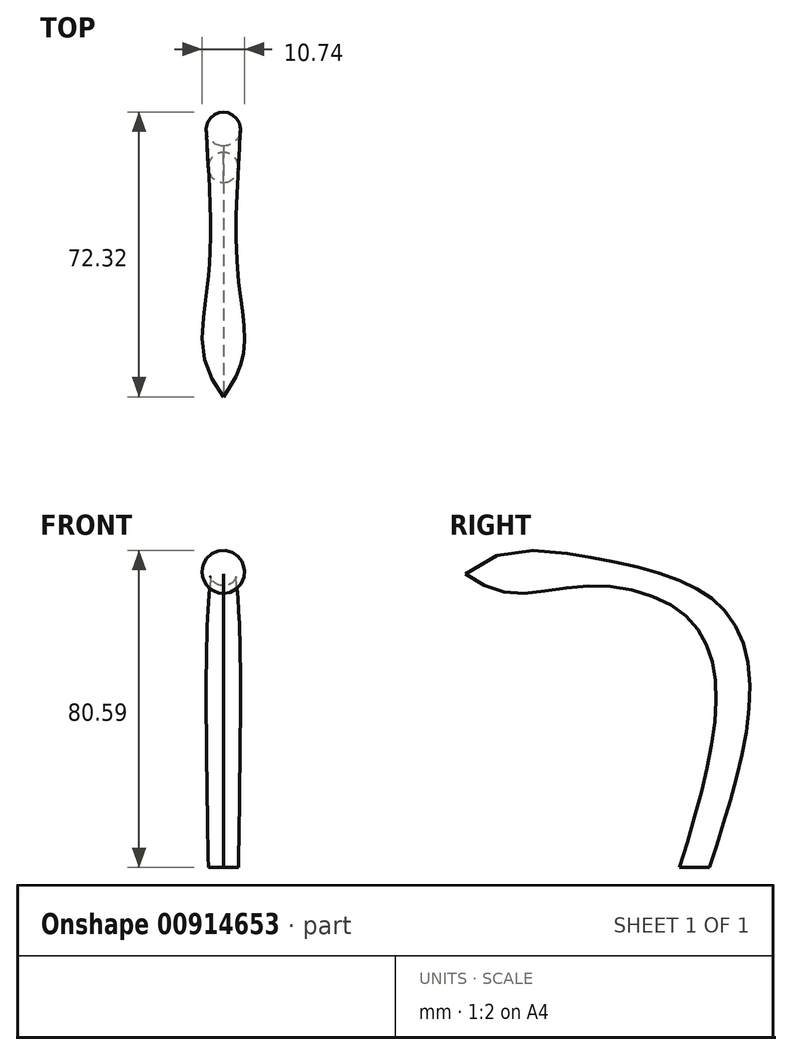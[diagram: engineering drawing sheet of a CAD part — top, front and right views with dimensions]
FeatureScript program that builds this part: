
annotation { "Feature Type Name" : "Feature", "Feature Type Description" : "" }
export const myFeature = defineFeature(function(context is Context, id is Id, definition is map)
    precondition{}
    {
        {
            var Q0;
            Q0=qCreatedBy(makeId("Top.planeOp"),FACE);
            var sketch = newSketch(context, id + "F0", { "sketchPlane" : qUnion([Q0])});
            skCircle(sketch, "E0", {"center": v(0, 0) * mm, "radius": 3.81 * mm});
            skSolve(sketch);
        }
        {
            var Q0;
            Q0=qCreatedBy(makeId("Right.planeOp"),FACE);
            var sketch = newSketch(context, id + "F1", { "sketchPlane" : qUnion([Q0])});
            skFitSpline(sketch, "E1", {"points": [v(0, 0) * mm, v(0, 66.6) * mm, v(-51.9, 74.72) * mm], "startDerivative": vector(29.22, 154.47) * mm, "endDerivative": vector(-136.3, -8.24) * mm});
            skFitSpline(sketch, "E2", {"points": [v(-51.9, 74.72) * mm, v(-57.65, 74.72) * mm], "startDerivative": vector(-5.75, 0) * mm, "endDerivative": vector(-5.75, 0) * mm});
            skPoint(sketch, "E3", {"position": v(-28.35, 75.54) * mm});
            skSolve(sketch);
        }
        {
            var Q0;
            Q0=sQuery(id+"F1.wireOp",VERTEX,"E1.1.internal");
            var Q1;
            Q1=sQuery(id+"F1.wireOp",EDGE,"E1");
            var Q2;
            Q2 = qBodyType(qCreatedBy(id + "F3" ,EDGE), BodyType.WIRE);
            cPlane(context, id + "F2", {"entities" : qUnion([Q0, Q1, Q2]), "cplaneType" : CPlaneType.CURVE_POINT, "offset" : 25.4 * mm, "width" : 152.4 * mm, "height" : 152.4 * mm});
        }
        {
            var Q0;
            Q0=qCreatedBy(id+"F2.planeOp",FACE);
            var sketch = newSketch(context, id + "F3", { "sketchPlane" : qUnion([Q0])});
            skCircle(sketch, "E4", {"center": v(0, 43.56) * mm, "radius": 3.81 * mm});
            skSolve(sketch);
        }
        {
            var Q0;
            Q0=sQuery(id+"F1.wireOp",VERTEX,"E1.end");
            var Q1;
            Q1=sQuery(id+"F1.wireOp",EDGE,"E1");
            cPlane(context, id + "F4", {"entities" : qUnion([Q0, Q1]), "cplaneType" : CPlaneType.CURVE_POINT, "offset" : 25.4 * mm, "width" : 152.4 * mm, "height" : 152.4 * mm});
        }
        {
            var Q0;
            Q0=qCreatedBy(id+"F4.planeOp",FACE);
            var sketch = newSketch(context, id + "F5", { "sketchPlane" : qUnion([Q0])});
            skCircle(sketch, "E5", {"center": v(0, 77.64) * mm, "radius": 3.81 * mm});
            skSolve(sketch);
        }
        {
            var Q0;
            Q0=qCreatedBy(id+"F4.planeOp",FACE);
            cPlane(context, id + "F6", {"entities" : qUnion([Q0]), "cplaneType" : CPlaneType.OFFSET, "offset" : 6.35 * mm, "width" : 152.4 * mm, "height" : 152.4 * mm});
        }
        {
            var Q0;
            Q0=qCreatedBy(id+"F6.planeOp",FACE);
            var sketch = newSketch(context, id + "F7", { "sketchPlane" : qUnion([Q0])});
            skCircle(sketch, "E6", {"center": v(0, 78) * mm, "radius": 1.27 * mm});
            skSolve(sketch);
        }
        {
            var Q0;
            Q0=sQuery(id+"F1.wireOp",VERTEX,"E3");
            var Q1;
            Q1=sQuery(id+"F1.wireOp",EDGE,"E1");
            cPlane(context, id + "F8", {"entities" : qUnion([Q0, Q1]), "cplaneType" : CPlaneType.CURVE_POINT, "offset" : 25.4 * mm, "width" : 152.4 * mm, "height" : 152.4 * mm});
        }
        {
            var Q0;
            Q0=qCreatedBy(id+"F8.planeOp",FACE);
            var sketch = newSketch(context, id + "F9", { "sketchPlane" : qUnion([Q0])});
            skCircle(sketch, "E7", {"center": v(0, 74.69) * mm, "radius": 3.81 * mm});
            skSolve(sketch);
        }
        {
            var Q0;
            Q0=makeQuery(id+"F0.imprint","IMPRINT",FACE,{"disambiguationData":[TD([[makeQuery(id+"F0.imprint","IMPRINT",EDGE,{"derivedFrom":sQuery(id+"F0.wireOp",EDGE,"E0")}),1.0]])]});
            var Q1;
            Q1=makeQuery(id+"F3.imprint","IMPRINT",FACE,{"disambiguationData":[TD([[makeQuery(id+"F3.imprint","IMPRINT",EDGE,{"derivedFrom":sQuery(id+"F3.wireOp",EDGE,"E4")}),1.0]])]});
            var Q2;
            Q2=makeQuery(id+"F9.imprint","IMPRINT",FACE,{"disambiguationData":[TD([[makeQuery(id+"F9.imprint","IMPRINT",EDGE,{"derivedFrom":sQuery(id+"F9.wireOp",EDGE,"E7")}),1.0]])]});
            var Q3;
            Q3=makeQuery(id+"F5.imprint","IMPRINT",FACE,{"disambiguationData":[TD([[makeQuery(id+"F5.imprint","IMPRINT",EDGE,{"derivedFrom":sQuery(id+"F5.wireOp",EDGE,"E5")}),1.0]])]});
            var Q4;
            Q4=sQuery(id+"F7.wireOp",VERTEX,"E6.center");
            loft(context, id + "F10", {"sheetProfilesArray" : [{ "sheetProfileEntities" : qUnion([Q0]) }, { "sheetProfileEntities" : qUnion([Q1]) }, { "sheetProfileEntities" : qUnion([Q2]) }, { "sheetProfileEntities" : qUnion([Q3]) }, { "sheetProfileEntities" : qUnion([Q4]) }]});
        }
    });
